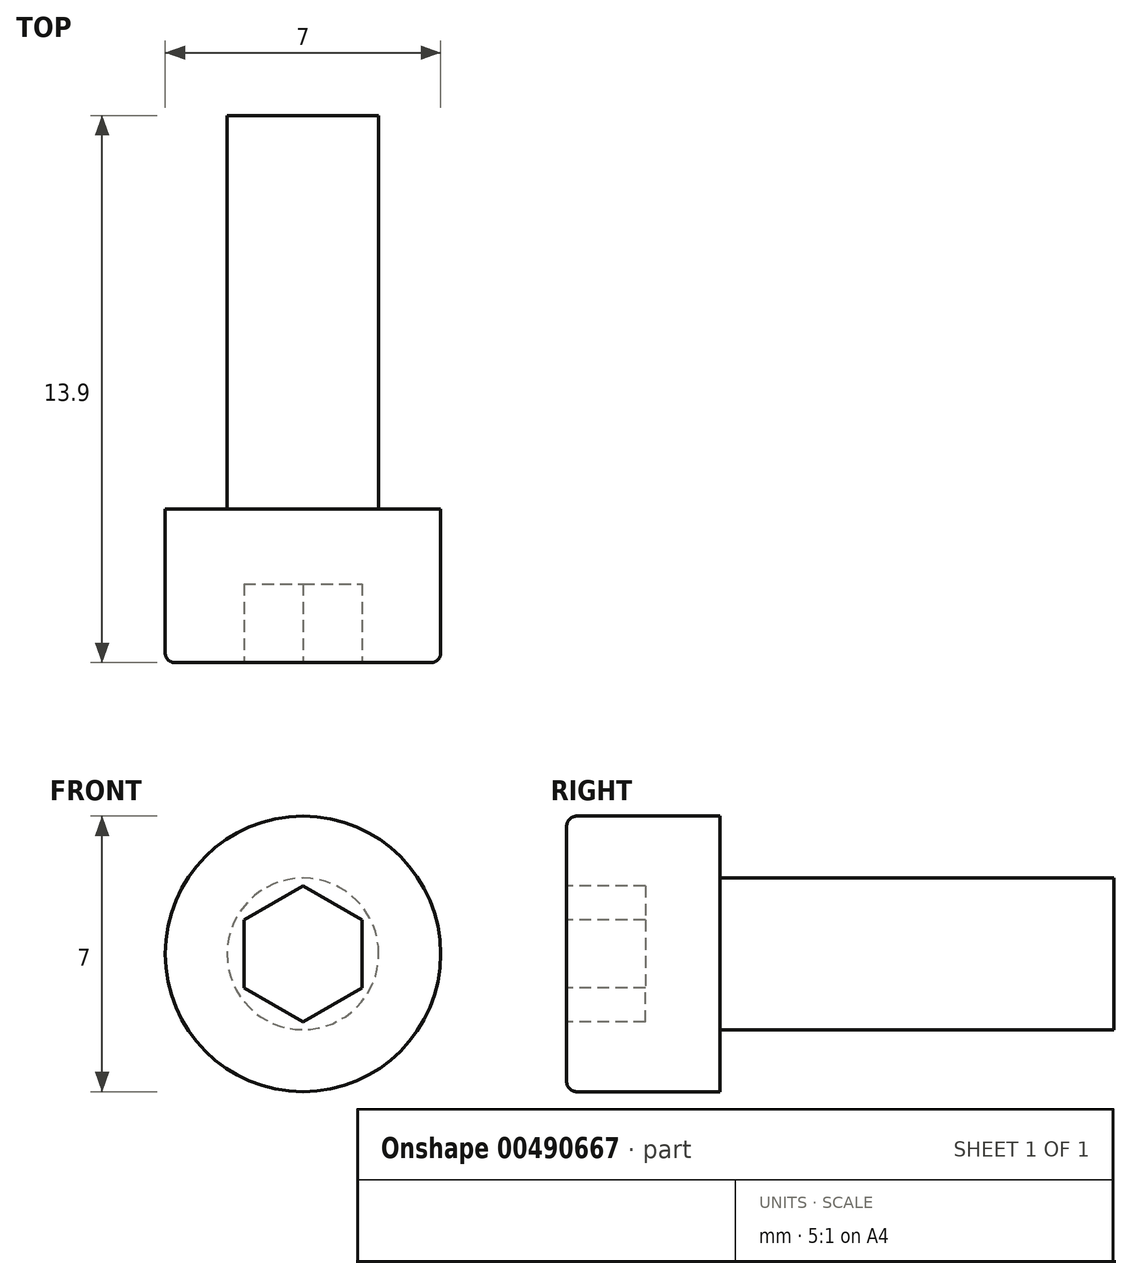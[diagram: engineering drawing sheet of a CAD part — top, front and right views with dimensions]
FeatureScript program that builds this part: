
annotation { "Feature Type Name" : "Feature", "Feature Type Description" : "" }
export const myFeature = defineFeature(function(context is Context, id is Id, definition is map)
    precondition{}
    {
        {
            var Q0;
            Q0=qCreatedBy(makeId("Front.planeOp"),FACE);
            var sketch = newSketch(context, id + "F0", { "sketchPlane" : qUnion([Q0])});
            skCircle(sketch, "E0", {"center": v(0, 0) * mm, "radius": 3.5 * mm});
            skCircle(sketch, "E1", {"center": v(0, 0) * mm, "radius": 1.93 * mm});
            skSolve(sketch);
        }
        {
            var Q0;
            Q0=makeQuery(id+"F0.imprint","IMPRINT",FACE,{"disambiguationData":[TD([[makeQuery(id+"F0.imprint","IMPRINT",EDGE,{"derivedFrom":sQuery(id+"F0.wireOp",EDGE,"E1")}),1.0]])]});
            var Q1;
            Q1=makeQuery(id+"F0.imprint","IMPRINT",FACE,{"disambiguationData":[TD([[makeQuery(id+"F0.imprint","IMPRINT",EDGE,{"derivedFrom":sQuery(id+"F0.wireOp",EDGE,"E0")}),1.0]])]});
            extrude(context, id + "F1", {"entities" : qUnion([Q0, Q1]), "depth" : 3.9 * mm});
        }
        {
            var Q0;
            Q0=makeQuery(id+"F0.imprint","IMPRINT",FACE,{"disambiguationData":[TD([[makeQuery(id+"F0.imprint","IMPRINT",EDGE,{"derivedFrom":sQuery(id+"F0.wireOp",EDGE,"E1")}),1.0]])]});
            extrude(context, id + "F2", {"entities" : qUnion([Q0]), "operationType" : NewBodyOperationType.ADD, "oppositeDirection" : true, "offsetDistance" : 25 * mm, "depth" : 10 * mm});
        }
        {
            var Q0;
            Q0=makeQuery(id+"F1.opExtrude","CAP_FACE",FACE,{"disambiguationData":[OSD([sQuery(id+"F0.wireOp",EDGE,"E0")])],"isStart":false});
            var sketch = newSketch(context, id + "F3", { "sketchPlane" : qUnion([Q0])});
            skCircle(sketch, "E2.cCircle", {"center": v(0, 0) * mm, "radius": 1.5 * mm, "construction": true});
            skLineSegment(sketch, "E2.0", {"start": v(1.5, 0.87) * mm, "end": v(1.5, -0.87) * mm});
            skLineSegment(sketch, "E2.1", {"start": v(1.5, -0.87) * mm, "end": v(0, -1.73) * mm});
            skLineSegment(sketch, "E2.2", {"start": v(0, -1.73) * mm, "end": v(-1.5, -0.87) * mm});
            skLineSegment(sketch, "E2.3", {"start": v(-1.5, -0.87) * mm, "end": v(-1.5, 0.87) * mm});
            skLineSegment(sketch, "E2.4", {"start": v(-1.5, 0.87) * mm, "end": v(0, 1.73) * mm});
            skLineSegment(sketch, "E2.5", {"start": v(0, 1.73) * mm, "end": v(1.5, 0.87) * mm});
            skPoint(sketch, "E2.0.midPoint", {"position": v(1.5, 0) * mm});
            skSolve(sketch);
        }
        {
            var Q0;
            Q0=makeQuery(id+"F3.imprint","IMPRINT",FACE,{"disambiguationData":[TD([[makeQuery(id+"F3.imprint","IMPRINT",EDGE,{"derivedFrom":sQuery(id+"F3.wireOp",EDGE,"E2.0")}),-1.0]])]});
            extrude(context, id + "F4", {"entities" : qUnion([Q0]), "operationType" : NewBodyOperationType.REMOVE, "oppositeDirection" : true, "depth" : 2 * mm});
        }
        {
            var Q0;
            Q0=makeQuery(id+"F1.opExtrude","CAP_EDGE",EDGE,{"disambiguationData":[OSD([sQuery(id+"F0.wireOp",EDGE,"E0")])],"isStart":false});
            fillet(context, id + "F5", {"entities" : qUnion([Q0]), "radius" : .25 * mm, "tangentPropagation" : true, "allowEdgeOverflow" : false});
        }
    });
